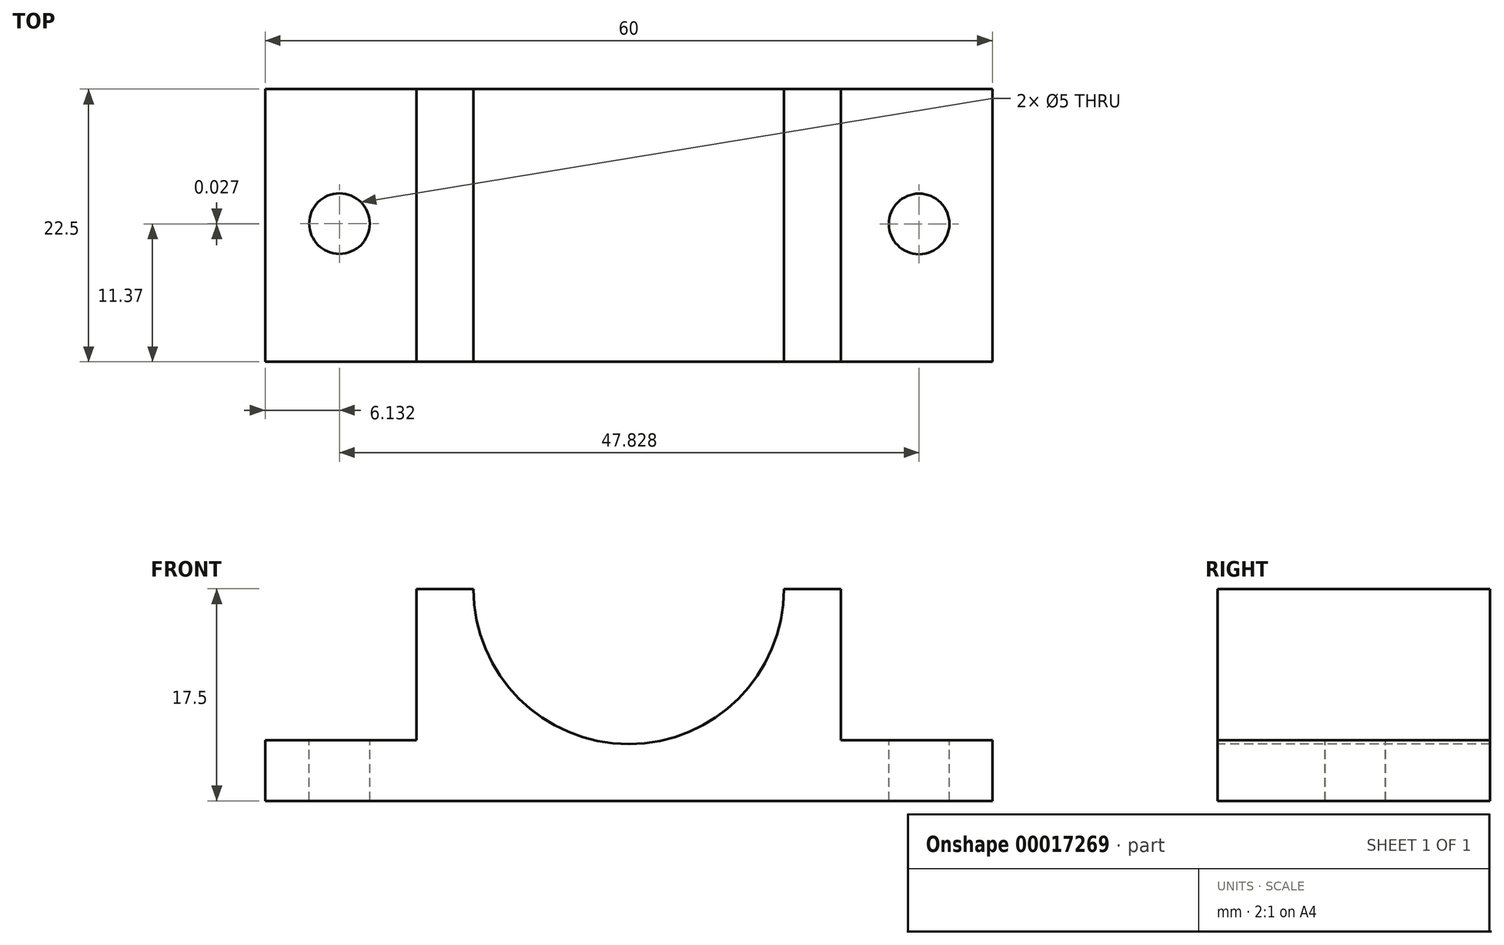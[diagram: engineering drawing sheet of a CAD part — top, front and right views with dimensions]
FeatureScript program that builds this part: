
annotation { "Feature Type Name" : "Feature", "Feature Type Description" : "" }
export const myFeature = defineFeature(function(context is Context, id is Id, definition is map)
    precondition{}
    {
        {
            var Q0;
            Q0=qCreatedBy(makeId("Front.planeOp"),FACE);
            var sketch = newSketch(context, id + "F0", { "sketchPlane" : qUnion([Q0])});
            skLineSegment(sketch, "E0", {"start": v(-31.5, -16.76) * mm, "end": v(28.5, -16.76) * mm});
            skLineSegment(sketch, "E1", {"start": v(28.5, -16.76) * mm, "end": v(28.5, -11.76) * mm});
            skLineSegment(sketch, "E2", {"start": v(28.5, -11.76) * mm, "end": v(16, -11.76) * mm});
            skLineSegment(sketch, "E3", {"start": v(16, -11.76) * mm, "end": v(16, 0.74) * mm});
            skLineSegment(sketch, "E4", {"start": v(16, 0.74) * mm, "end": v(-19, 0.74) * mm});
            skLineSegment(sketch, "E5", {"start": v(-19, 0.74) * mm, "end": v(-19, -11.76) * mm});
            skLineSegment(sketch, "E6", {"start": v(-19, -11.76) * mm, "end": v(-31.5, -11.76) * mm});
            skLineSegment(sketch, "E7", {"start": v(-31.5, -11.76) * mm, "end": v(-31.5, -16.76) * mm});
            skSolve(sketch);
        }
        {
            var Q0;
            Q0=makeQuery(id+"F0.imprint","IMPRINT",FACE,{"disambiguationData":[TD([[makeQuery(id+"F0.imprint","IMPRINT",EDGE,{"derivedFrom":sQuery(id+"F0.wireOp",EDGE,"E0")}),1.0]])]});
            extrude(context, id + "F1", {"entities" : qUnion([Q0]), "depth" : 22.5 * mm});
        }
        {
            var Q0;
            Q0=makeQuery(id+"F1.opExtrude","CAP_FACE",FACE,{"disambiguationData":[OSD([sQuery(id+"F0.wireOp",EDGE,"E0"),sQuery(id+"F0.wireOp",EDGE,"E1"),sQuery(id+"F0.wireOp",EDGE,"E2"),sQuery(id+"F0.wireOp",EDGE,"E3"),sQuery(id+"F0.wireOp",EDGE,"E4"),sQuery(id+"F0.wireOp",EDGE,"E5"),sQuery(id+"F0.wireOp",EDGE,"E6"),sQuery(id+"F0.wireOp",EDGE,"E7")])],"isStart":false});
            var sketch = newSketch(context, id + "F2", { "sketchPlane" : qUnion([Q0])});
            skCircle(sketch, "E8", {"center": v(-1.5, 0.74) * mm, "radius": 12.8 * mm});
            skSolve(sketch);
        }
        {
            var Q0;
            Q0 = qSketchRegion(id + "F2", true);
            extrude(context, id + "F3", {"entities" : qUnion([Q0]), "operationType" : NewBodyOperationType.REMOVE, "endBound" : BoundingType.THROUGH_ALL, "oppositeDirection" : true, "depth" : 25 * mm});
        }
        {
            var Q0;
            Q0=makeQuery(id+"F1.opExtrude","SWEPT_FACE",FACE,{"disambiguationData":[OSD([sQuery(id+"F0.wireOp",EDGE,"E6")])]});
            var sketch = newSketch(context, id + "F4", { "sketchPlane" : qUnion([Q0])});
            skCircle(sketch, "E9", {"center": v(-25.36, -11.1) * mm, "radius": 2.5 * mm});
            skSolve(sketch);
        }
        {
            var Q0;
            Q0 = qSketchRegion(id + "F4", true);
            extrude(context, id + "F5", {"entities" : qUnion([Q0]), "operationType" : NewBodyOperationType.REMOVE, "endBound" : BoundingType.THROUGH_ALL, "oppositeDirection" : true, "depth" : 25 * mm});
        }
        {
            var Q0;
            Q0=makeQuery(id+"F1.opExtrude","SWEPT_FACE",FACE,{"disambiguationData":[OSD([sQuery(id+"F0.wireOp",EDGE,"E2")])]});
            var sketch = newSketch(context, id + "F6", { "sketchPlane" : qUnion([Q0])});
            skCircle(sketch, "E10", {"center": v(22.47, -11.13) * mm, "radius": 2.5 * mm});
            skSolve(sketch);
        }
        {
            var Q0;
            Q0 = qSketchRegion(id + "F6", true);
            extrude(context, id + "F7", {"entities" : qUnion([Q0]), "operationType" : NewBodyOperationType.REMOVE, "endBound" : BoundingType.THROUGH_ALL, "oppositeDirection" : true, "depth" : 25 * mm});
        }
    });
